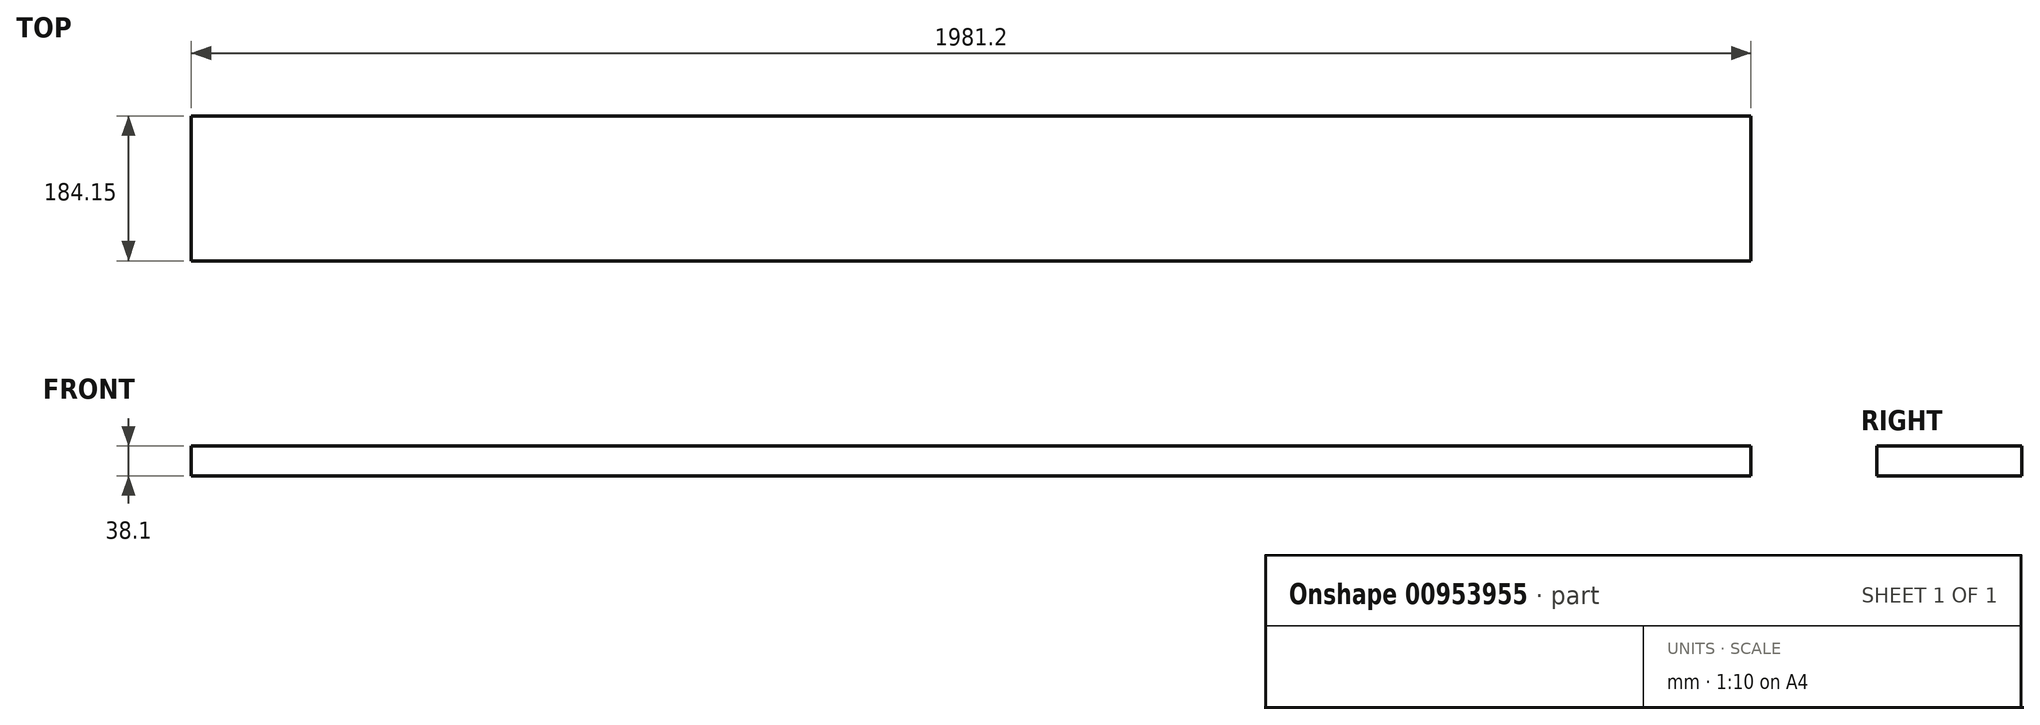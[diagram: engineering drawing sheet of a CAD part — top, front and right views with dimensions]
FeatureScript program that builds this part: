
annotation { "Feature Type Name" : "Feature", "Feature Type Description" : "" }
export const myFeature = defineFeature(function(context is Context, id is Id, definition is map)
    precondition{}
    {
        {
            var Q0;
            Q0=qCreatedBy(makeId("Top.planeOp"),FACE);
            var sketch = newSketch(context, id + "F0", { "sketchPlane" : qUnion([Q0])});
            skLineSegment(sketch, "E0.bottom", {"start": v(0, 0) * mm, "end": v(1981.2, 0) * mm});
            skLineSegment(sketch, "E0.top", {"start": v(0, 184.15) * mm, "end": v(1981.2, 184.15) * mm});
            skLineSegment(sketch, "E0.left", {"start": v(0, 0) * mm, "end": v(0, 184.15) * mm});
            skLineSegment(sketch, "E0.right", {"start": v(1981.2, 0) * mm, "end": v(1981.2, 184.15) * mm});
            skSolve(sketch);
        }
        {
            var Q0;
            Q0=qSketchRegion(id+"F0",true);
            extrude(context, id + "F1", {"entities" : qUnion([Q0]), "depth" : 38.1 * mm, "offsetDistance" : 25.4 * mm});
        }
    });
